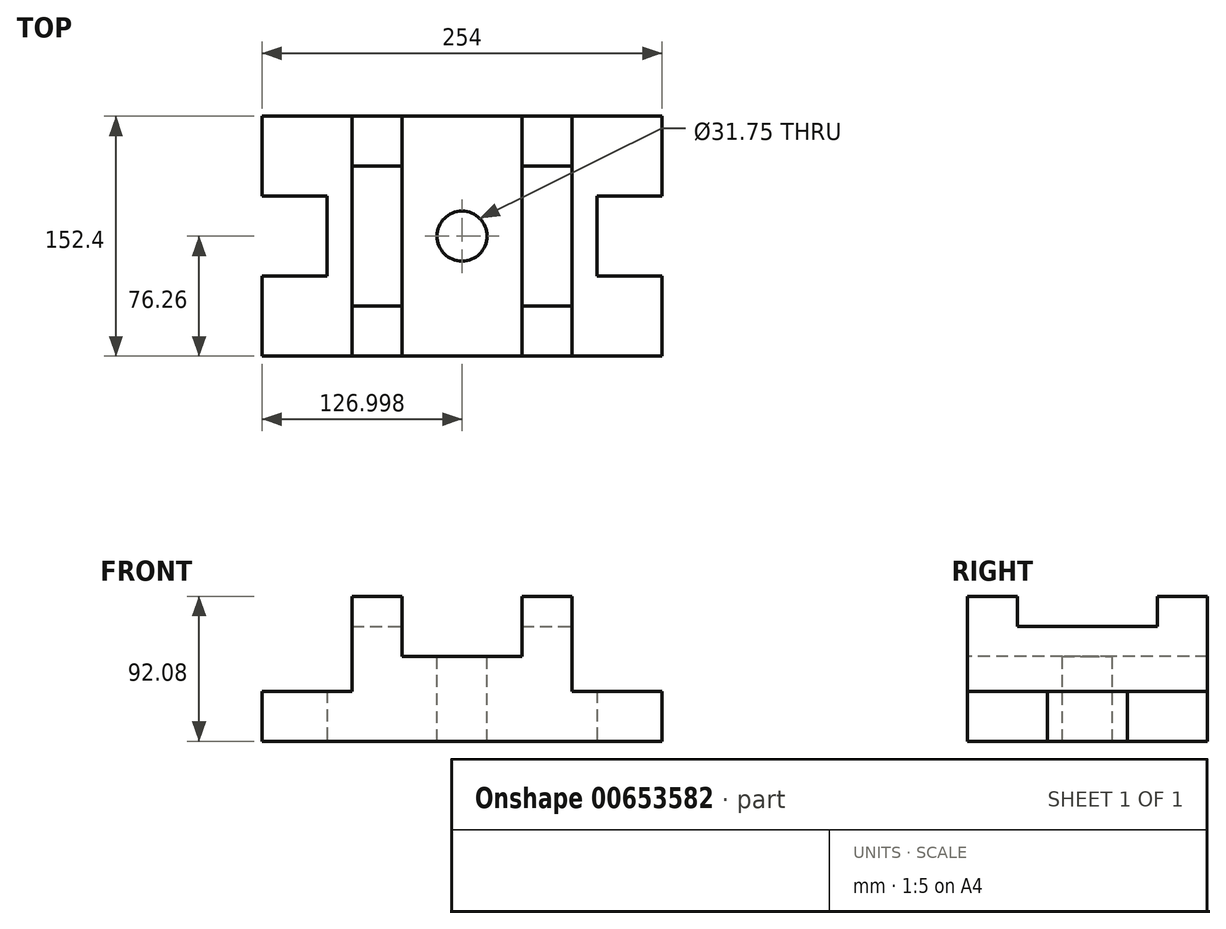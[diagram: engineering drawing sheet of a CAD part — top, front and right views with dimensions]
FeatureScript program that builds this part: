
annotation { "Feature Type Name" : "Feature", "Feature Type Description" : "" }
export const myFeature = defineFeature(function(context is Context, id is Id, definition is map)
    precondition{}
    {
        {
            var Q0;
            Q0=qCreatedBy(makeId("Top.planeOp"),FACE);
            var sketch = newSketch(context, id + "F0", { "sketchPlane" : qUnion([Q0])});
            skLineSegment(sketch, "E0.bottom", {"start": v(-89.42, 76.14) * mm, "end": v(164.58, 76.14) * mm});
            skLineSegment(sketch, "E0.top", {"start": v(-89.42, -76.26) * mm, "end": v(164.58, -76.26) * mm});
            skLineSegment(sketch, "E0.left", {"start": v(-89.42, 76.14) * mm, "end": v(-89.42, -76.26) * mm});
            skLineSegment(sketch, "E0.right", {"start": v(164.58, 76.14) * mm, "end": v(164.58, -76.26) * mm});
            skSolve(sketch);
        }
        {
            var Q0;
            Q0 = qSketchRegion(id + "F0", true);
            extrude(context, id + "F1", {"entities" : qUnion([Q0]), "depth" : 92.07 * mm, "offsetDistance" : 25.4 * mm});
        }
        {
            var Q0;
            Q0=makeQuery(id+"F1.opExtrude","SWEPT_FACE",FACE,{"disambiguationData":[OSD([sQuery(id+"F0.wireOp",EDGE,"E0.top")])]});
            var sketch = newSketch(context, id + "F2", { "sketchPlane" : qUnion([Q0])});
            skLineSegment(sketch, "E1.bottom", {"start": v(164.58, 92.08) * mm, "end": v(107.43, 92.08) * mm});
            skLineSegment(sketch, "E1.top", {"start": v(164.58, 31.75) * mm, "end": v(107.43, 31.75) * mm});
            skLineSegment(sketch, "E1.left", {"start": v(164.58, 92.08) * mm, "end": v(164.58, 31.75) * mm});
            skLineSegment(sketch, "E1.right", {"start": v(107.43, 92.08) * mm, "end": v(107.43, 31.75) * mm});
            skLineSegment(sketch, "E2.bottom", {"start": v(-89.42, 31.75) * mm, "end": v(-32.27, 31.75) * mm});
            skLineSegment(sketch, "E2.top", {"start": v(-89.42, 92.08) * mm, "end": v(-32.27, 92.08) * mm});
            skLineSegment(sketch, "E2.left", {"start": v(-89.42, 31.75) * mm, "end": v(-89.42, 92.08) * mm});
            skLineSegment(sketch, "E2.right", {"start": v(-32.27, 31.75) * mm, "end": v(-32.27, 92.08) * mm});
            skSolve(sketch);
        }
        {
            var Q0;
            Q0=makeQuery(id+"F2.imprint","IMPRINT",FACE,{"disambiguationData":[TD([[makeQuery(id+"F2.imprint","IMPRINT",EDGE,{"derivedFrom":sQuery(id+"F2.wireOp",EDGE,"E2.bottom")}),1.0]])]});
            var Q1;
            Q1=makeQuery(id+"F2.imprint","IMPRINT",FACE,{"disambiguationData":[TD([[makeQuery(id+"F2.imprint","IMPRINT",EDGE,{"derivedFrom":sQuery(id+"F2.wireOp",EDGE,"E1.bottom")}),-1.0]])]});
            extrude(context, id + "F3", {"entities" : qUnion([Q0, Q1]), "operationType" : NewBodyOperationType.REMOVE, "endBound" : BoundingType.THROUGH_ALL, "oppositeDirection" : true, "depth" : 25.4 * mm, "offsetDistance" : 25.4 * mm});
        }
        {
            var Q0;
            Q0=makeQuery(id+"F1.opExtrude","SWEPT_FACE",FACE,{"disambiguationData":[OSD([sQuery(id+"F0.wireOp",EDGE,"E0.right")])]});
            var sketch = newSketch(context, id + "F4", { "sketchPlane" : qUnion([Q0])});
            skLineSegment(sketch, "E3.bottom", {"start": v(-25.46, 31.75) * mm, "end": v(25.34, 31.75) * mm});
            skLineSegment(sketch, "E3.top", {"start": v(-25.46, 0) * mm, "end": v(25.34, 0) * mm});
            skLineSegment(sketch, "E3.left", {"start": v(-25.46, 31.75) * mm, "end": v(-25.46, 0) * mm});
            skLineSegment(sketch, "E3.right", {"start": v(25.34, 31.75) * mm, "end": v(25.34, 0) * mm});
            skSolve(sketch);
        }
        {
            var Q0;
            Q0=makeQuery(id+"F4.imprint","IMPRINT",FACE,{"disambiguationData":[TD([[makeQuery(id+"F4.imprint","IMPRINT",EDGE,{"derivedFrom":sQuery(id+"F4.wireOp",EDGE,"E3.bottom")}),1.0]])]});
            extrude(context, id + "F5", {"entities" : qUnion([Q0]), "operationType" : NewBodyOperationType.REMOVE, "oppositeDirection" : true, "depth" : 41.27 * mm, "offsetDistance" : 25.4 * mm});
        }
        {
            var Q0;
            Q0=makeQuery(id+"F1.opExtrude","SWEPT_FACE",FACE,{"disambiguationData":[OSD([sQuery(id+"F0.wireOp",EDGE,"E0.left")])]});
            var sketch = newSketch(context, id + "F6", { "sketchPlane" : qUnion([Q0])});
            skLineSegment(sketch, "E4.bottom", {"start": v(-25.34, 31.75) * mm, "end": v(25.46, 31.75) * mm});
            skLineSegment(sketch, "E4.top", {"start": v(-25.34, 0) * mm, "end": v(25.46, 0) * mm});
            skLineSegment(sketch, "E4.left", {"start": v(-25.34, 31.75) * mm, "end": v(-25.34, 0) * mm});
            skLineSegment(sketch, "E4.right", {"start": v(25.46, 31.75) * mm, "end": v(25.46, 0) * mm});
            skSolve(sketch);
        }
        {
            var Q0;
            Q0=makeQuery(id+"F6.imprint","IMPRINT",FACE,{"disambiguationData":[TD([[makeQuery(id+"F6.imprint","IMPRINT",EDGE,{"derivedFrom":sQuery(id+"F6.wireOp",EDGE,"E4.bottom")}),-1.0]])]});
            extrude(context, id + "F7", {"entities" : qUnion([Q0]), "operationType" : NewBodyOperationType.REMOVE, "oppositeDirection" : true, "depth" : 41.27 * mm, "offsetDistance" : 25.4 * mm});
        }
        {
            var Q0;
            Q0=makeQuery(id+"F1.opExtrude","SWEPT_FACE",FACE,{"disambiguationData":[OSD([sQuery(id+"F0.wireOp",EDGE,"E0.top")])]});
            var sketch = newSketch(context, id + "F8", { "sketchPlane" : qUnion([Q0])});
            skLineSegment(sketch, "E5.bottom", {"start": v(-0.52, 92.08) * mm, "end": v(75.68, 92.08) * mm});
            skLineSegment(sketch, "E5.top", {"start": v(-0.52, 53.98) * mm, "end": v(75.68, 53.98) * mm});
            skLineSegment(sketch, "E5.left", {"start": v(-0.52, 92.08) * mm, "end": v(-0.52, 53.97) * mm});
            skLineSegment(sketch, "E5.right", {"start": v(75.68, 92.08) * mm, "end": v(75.68, 53.97) * mm});
            skSolve(sketch);
        }
        {
            var Q0;
            Q0=makeQuery(id+"F8.imprint","IMPRINT",FACE,{"disambiguationData":[TD([[makeQuery(id+"F8.imprint","IMPRINT",EDGE,{"derivedFrom":sQuery(id+"F8.wireOp",EDGE,"E5.bottom")}),-1.0]])]});
            extrude(context, id + "F9", {"entities" : qUnion([Q0]), "operationType" : NewBodyOperationType.REMOVE, "endBound" : BoundingType.THROUGH_ALL, "oppositeDirection" : true, "depth" : 25.4 * mm, "offsetDistance" : 25.4 * mm});
        }
        {
            var Q0;
            Q0=makeQuery(id+"F3.boolean.opBoolean","COPY",FACE,{"derivedFrom":makeQuery(id+"F3.opExtrude","SWEPT_FACE",FACE,{"disambiguationData":[OSD([sQuery(id+"F2.wireOp",EDGE,"E1.right")])]})});
            var sketch = newSketch(context, id + "F10", { "sketchPlane" : qUnion([Q0])});
            skLineSegment(sketch, "E6.bottom", {"start": v(-44.51, 92.08) * mm, "end": v(44.39, 92.08) * mm});
            skLineSegment(sketch, "E6.top", {"start": v(-44.51, 73.03) * mm, "end": v(44.39, 73.03) * mm});
            skLineSegment(sketch, "E6.left", {"start": v(-44.51, 92.08) * mm, "end": v(-44.51, 73.03) * mm});
            skLineSegment(sketch, "E6.right", {"start": v(44.39, 92.08) * mm, "end": v(44.39, 73.03) * mm});
            skSolve(sketch);
        }
        {
            var Q0;
            Q0=makeQuery(id+"F10.imprint","IMPRINT",FACE,{"disambiguationData":[TD([[makeQuery(id+"F10.imprint","IMPRINT",EDGE,{"derivedFrom":sQuery(id+"F10.wireOp",EDGE,"E6.bottom")}),1.0]])]});
            extrude(context, id + "F11", {"entities" : qUnion([Q0]), "operationType" : NewBodyOperationType.REMOVE, "endBound" : BoundingType.THROUGH_ALL, "oppositeDirection" : true, "depth" : 25.4 * mm, "offsetDistance" : 25.4 * mm});
        }
        {
            var Q0;
            Q0=makeQuery(id+"F9.boolean.opBoolean","COPY",FACE,{"derivedFrom":makeQuery(id+"F9.opExtrude","SWEPT_FACE",FACE,{"disambiguationData":[OSD([sQuery(id+"F8.wireOp",EDGE,"E5.top")])]})});
            var sketch = newSketch(context, id + "F12", { "sketchPlane" : qUnion([Q0])});
            skCircle(sketch, "E7", {"center": v(37.58, 0) * mm, "radius": 15.88 * mm});
            skSolve(sketch);
        }
        {
            var Q0;
            Q0=makeQuery(id+"F12.imprint","IMPRINT",FACE,{"disambiguationData":[TD([[makeQuery(id+"F12.imprint","IMPRINT",EDGE,{"derivedFrom":sQuery(id+"F12.wireOp",EDGE,"E7")}),1.0]])]});
            extrude(context, id + "F13", {"entities" : qUnion([Q0]), "operationType" : NewBodyOperationType.REMOVE, "endBound" : BoundingType.THROUGH_ALL, "oppositeDirection" : true, "depth" : 25.4 * mm, "offsetDistance" : 25.4 * mm});
        }
    });
